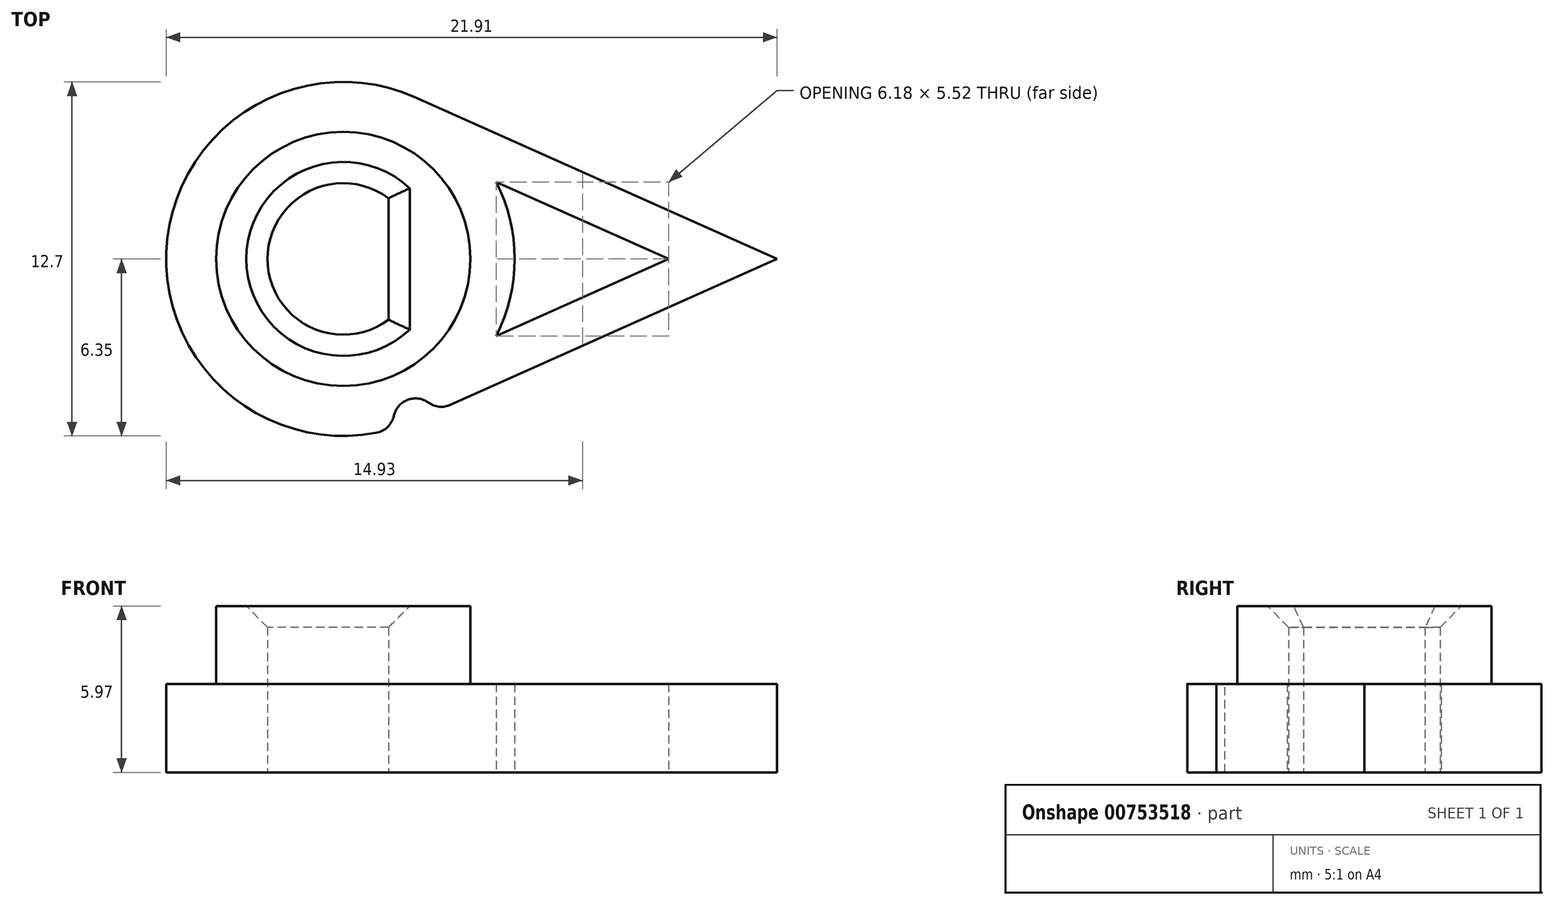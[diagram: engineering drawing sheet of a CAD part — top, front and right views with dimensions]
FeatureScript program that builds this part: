
annotation { "Feature Type Name" : "Feature", "Feature Type Description" : "" }
export const myFeature = defineFeature(function(context is Context, id is Id, definition is map)
    precondition{}
    {
        {
            var Q0;
            Q0=qCreatedBy(makeId("Top.planeOp"),FACE);
            var sketch = newSketch(context, id + "F0", { "sketchPlane" : qUnion([Q0]), "disableImprinting" : false});
            skArc(sketch, "E0", {"start": v(2.6, 5.8) * mm, "mid": v(-6.35, 0) * mm, "end": v(2.6, -5.8) * mm});
            skLineSegment(sketch, "E1", {"start": v(2.6, 5.8) * mm, "end": v(15.56, 0) * mm});
            skLineSegment(sketch, "E2", {"start": v(15.56, 0) * mm, "end": v(2.6, -5.8) * mm});
            skCircle(sketch, "E3", {"center": v(0, 0) * mm, "radius": 4.56 * mm});
            skLineSegment(sketch, "E4.bottom", {"start": v(-1.63, 2.18) * mm, "end": v(1.63, 2.18) * mm, "construction": true});
            skLineSegment(sketch, "E4.top", {"start": v(-1.63, -2.18) * mm, "end": v(1.63, -2.18) * mm, "construction": true});
            skLineSegment(sketch, "E4.left", {"start": v(-1.63, 2.18) * mm, "end": v(-1.63, -2.18) * mm, "construction": true});
            skLineSegment(sketch, "E4.right", {"start": v(1.63, 2.18) * mm, "end": v(1.63, -2.18) * mm});
            skArc(sketch, "E5", {"start": v(1.63, 2.18) * mm, "mid": v(0, 2.72) * mm, "end": v(-1.63, 2.18) * mm});
            skArc(sketch, "E6", {"start": v(-1.63, -2.18) * mm, "mid": v(0, -2.72) * mm, "end": v(1.63, -2.18) * mm});
            skArc(sketch, "E7", {"start": v(5.5, -2.76) * mm, "mid": v(6.15, 0) * mm, "end": v(5.5, 2.76) * mm});
            skLineSegment(sketch, "E8", {"start": v(5.5, -2.76) * mm, "end": v(11.67, 0) * mm});
            skLineSegment(sketch, "E9", {"start": v(11.67, 0) * mm, "end": v(5.5, 2.76) * mm});
            skLineSegment(sketch, "E10", {"start": v(5.5, 2.76) * mm, "end": v(5.5, -2.76) * mm, "construction": true});
            skArc(sketch, "E11", {"start": v(-1.63, 2.18) * mm, "mid": v(-2.72, 0) * mm, "end": v(-1.63, -2.18) * mm});
            skSolve(sketch);
        }
        {
            var Q0;
            Q0=makeQuery(id+"F0.imprint","IMPRINT",FACE,{"disambiguationData":[TD([[makeQuery(id+"F0.imprint","IMPRINT",EDGE,{"derivedFrom":sQuery(id+"F0.wireOp",EDGE,"E3")}),1.0]])]});
            extrude(context, id + "F1", {"entities" : qUnion([Q0]), "depth" : 5.97 * mm, "offsetDistance" : 25.4 * mm});
        }
        {
            var Q0;
            Q0=makeQuery(id+"F0.imprint","IMPRINT",FACE,{"disambiguationData":[TD([[makeQuery(id+"F0.imprint","IMPRINT",EDGE,{"derivedFrom":sQuery(id+"F0.wireOp",EDGE,"E0")}),1.0]])]});
            extrude(context, id + "F2", {"entities" : qUnion([Q0]), "operationType" : NewBodyOperationType.ADD, "depth" : 3.17 * mm, "offsetDistance" : 25.4 * mm});
        }
        {
            var Q0;
            Q0=makeQuery(id+"F2.opExtrude","CAP_FACE",FACE,{"disambiguationData":[OSD([sQuery(id+"F0.wireOp",EDGE,"E0"),sQuery(id+"F0.wireOp",EDGE,"E1"),sQuery(id+"F0.wireOp",EDGE,"E2"),sQuery(id+"F0.wireOp",EDGE,"E3"),sQuery(id+"F0.wireOp",EDGE,"E7"),sQuery(id+"F0.wireOp",EDGE,"E8"),sQuery(id+"F0.wireOp",EDGE,"E9")])],"isStart":false});
            var sketch = newSketch(context, id + "F3", { "sketchPlane" : qUnion([Q0])});
            skCircle(sketch, "E12", {"center": v(2.6, -5.8) * mm, "radius": 0.8 * mm});
            skSolve(sketch);
        }
        {
            var Q0;
            {var subQ0=sQuery(id+"F3.wireOp",EDGE,"E12");var subQ1=makeQuery(id+"F2.opExtrude","CAP_EDGE",EDGE,{"disambiguationData":[OSD([sQuery(id+"F0.wireOp",EDGE,"E0")])],"isStart":false});var subQ2=makeQuery(id+"F3.imprint","INTERSECT",VERTEX,{"derivedFrom":[subQ1,subQ0]});Q0=makeQuery(id+"F3.imprint","IMPRINT",FACE,{"disambiguationData":[TD([[makeQuery(id+"F3.imprint","IMPRINT",EDGE,{"disambiguationData":[TD([[subQ2,1.0]])],"derivedFrom":subQ0}),1.0]])]});}
            var Q1;
            {var subQ0=sQuery(id+"F3.wireOp",EDGE,"E12");var subQ1=makeQuery(id+"F2.opExtrude","CAP_EDGE",EDGE,{"disambiguationData":[OSD([sQuery(id+"F0.wireOp",EDGE,"E0")])],"isStart":false});var subQ2=makeQuery(id+"F3.imprint","INTERSECT",VERTEX,{"derivedFrom":[subQ1,subQ0]});Q1=makeQuery(id+"F3.imprint","IMPRINT",FACE,{"disambiguationData":[TD([[makeQuery(id+"F3.imprint","IMPRINT",EDGE,{"disambiguationData":[TD([[subQ2,-1.0]])],"derivedFrom":subQ0}),1.0]])]});}
            var Q2;
            {var subQ0=sQuery(id+"F0.wireOp",EDGE,"E3");Q2=makeQuery(id+"F2.boolean.opBoolean","MERGE",FACE,{"derivedFrom":[makeQuery(id+"F1.opExtrude","CAP_FACE",FACE,{"disambiguationData":[OSD([subQ0,sQuery(id+"F0.wireOp",EDGE,"E4.left"),sQuery(id+"F0.wireOp",EDGE,"E4.right"),sQuery(id+"F0.wireOp",EDGE,"E5"),sQuery(id+"F0.wireOp",EDGE,"E6")])],"isStart":true}),makeQuery(id+"F2.opExtrude","CAP_FACE",FACE,{"disambiguationData":[OSD([sQuery(id+"F0.wireOp",EDGE,"E0"),sQuery(id+"F0.wireOp",EDGE,"E1"),sQuery(id+"F0.wireOp",EDGE,"E2"),subQ0,sQuery(id+"F0.wireOp",EDGE,"E7"),sQuery(id+"F0.wireOp",EDGE,"E8"),sQuery(id+"F0.wireOp",EDGE,"E9")])],"isStart":true})]});}
            extrude(context, id + "F4", {"entities" : qUnion([Q0, Q1]), "operationType" : NewBodyOperationType.REMOVE, "endBound" : BoundingType.UP_TO_SURFACE, "oppositeDirection" : true, "depth" : 25.4 * mm, "endBoundEntityFace" : qUnion([Q2]), "offsetDistance" : 25.4 * mm});
        }
        {
            var Q0;
            Q0=makeQuery(id+"F4.boolean.opBoolean","INTERSECT",EDGE,{"derivedFrom":[makeQuery(id+"F2.opExtrude","SWEPT_FACE",FACE,{"disambiguationData":[OSD([sQuery(id+"F0.wireOp",EDGE,"E0")])]}),makeQuery(id+"F4.opExtrude","SWEPT_FACE",FACE,{"disambiguationData":[OSD([sQuery(id+"F3.wireOp",EDGE,"E12")])]})]});
            var Q1;
            Q1=makeQuery(id+"F4.boolean.opBoolean","INTERSECT",EDGE,{"derivedFrom":[makeQuery(id+"F2.opExtrude","SWEPT_FACE",FACE,{"disambiguationData":[OSD([sQuery(id+"F0.wireOp",EDGE,"E2")])]}),makeQuery(id+"F4.opExtrude","SWEPT_FACE",FACE,{"disambiguationData":[OSD([sQuery(id+"F3.wireOp",EDGE,"E12")])]})]});
            fillet(context, id + "F5", {"entities" : qUnion([Q0, Q1]), "radius" : 0.8 * mm, "allowEdgeOverflow" : false});
        }
        {
            var Q0;
            Q0=makeQuery(id+"F1.opExtrude","CAP_EDGE",EDGE,{"disambiguationData":[OSD([sQuery(id+"F0.wireOp",EDGE,"E6")])],"isStart":false});
            var Q1;
            Q1=makeQuery(id+"F1.opExtrude","CAP_EDGE",EDGE,{"disambiguationData":[OSD([sQuery(id+"F0.wireOp",EDGE,"E5")])],"isStart":false});
            var Q2;
            Q2=makeQuery(id+"F1.opExtrude","CAP_EDGE",EDGE,{"disambiguationData":[OSD([sQuery(id+"F0.wireOp",EDGE,"E4.left")])],"isStart":false});
            var Q3;
            Q3=makeQuery(id+"F1.opExtrude","CAP_EDGE",EDGE,{"disambiguationData":[OSD([sQuery(id+"F0.wireOp",EDGE,"E4.right")])],"isStart":false});
            chamfer(context, id + "F6", {"entities" : qUnion([Q0, Q1, Q2, Q3]), "width" : 0.76 * mm, "tangentPropagation" : true});
        }
    });
